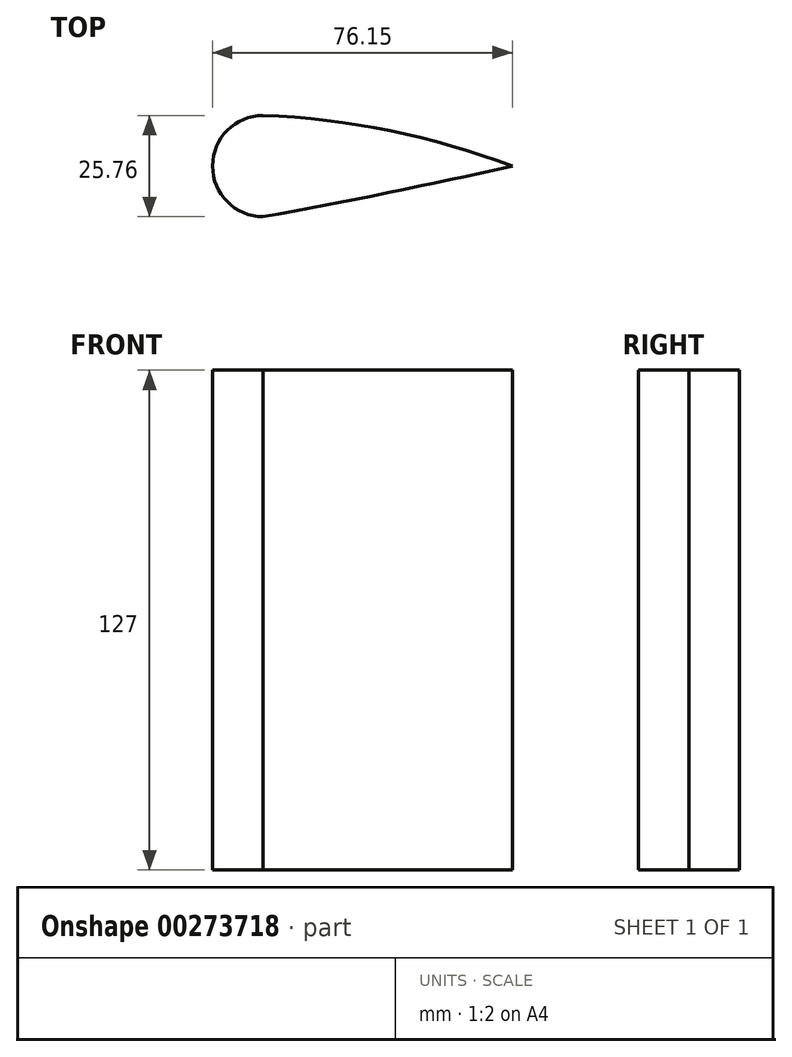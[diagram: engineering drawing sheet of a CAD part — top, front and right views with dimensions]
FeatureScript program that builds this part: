
annotation { "Feature Type Name" : "Feature", "Feature Type Description" : "" }
export const myFeature = defineFeature(function(context is Context, id is Id, definition is map)
    precondition{}
    {
        {
            var Q0;
            Q0=qCreatedBy(makeId("Top.planeOp"),FACE);
            var sketch = newSketch(context, id + "F0", { "sketchPlane" : qUnion([Q0])});
            skArc(sketch, "E0", {"start": v(0, 0) * mm, "mid": v(3.76, -9.1) * mm, "end": v(12.84, -12.88) * mm});
            skArc(sketch, "E1", {"start": v(0, 0) * mm, "mid": v(3.77, 9.1) * mm, "end": v(12.88, 12.88) * mm});
            skArc(sketch, "E2", {"start": v(76.15, 0) * mm, "mid": v(45.03, 8.97) * mm, "end": v(12.88, 12.88) * mm});
            skArc(sketch, "E3", {"start": v(12.84, -12.88) * mm, "mid": v(44.56, -6.77) * mm, "end": v(76.15, 0) * mm});
            skSolve(sketch);
        }
        {
            var Q0;
            Q0=makeQuery(id+"F0.imprint","IMPRINT",FACE,{"disambiguationData":[TD([[makeQuery(id+"F0.imprint","IMPRINT",EDGE,{"derivedFrom":sQuery(id+"F0.wireOp",EDGE,"E0")}),1.0]])]});
            extrude(context, id + "F1", {"entities" : qUnion([Q0]), "depth" : 127 * mm});
        }
    });
